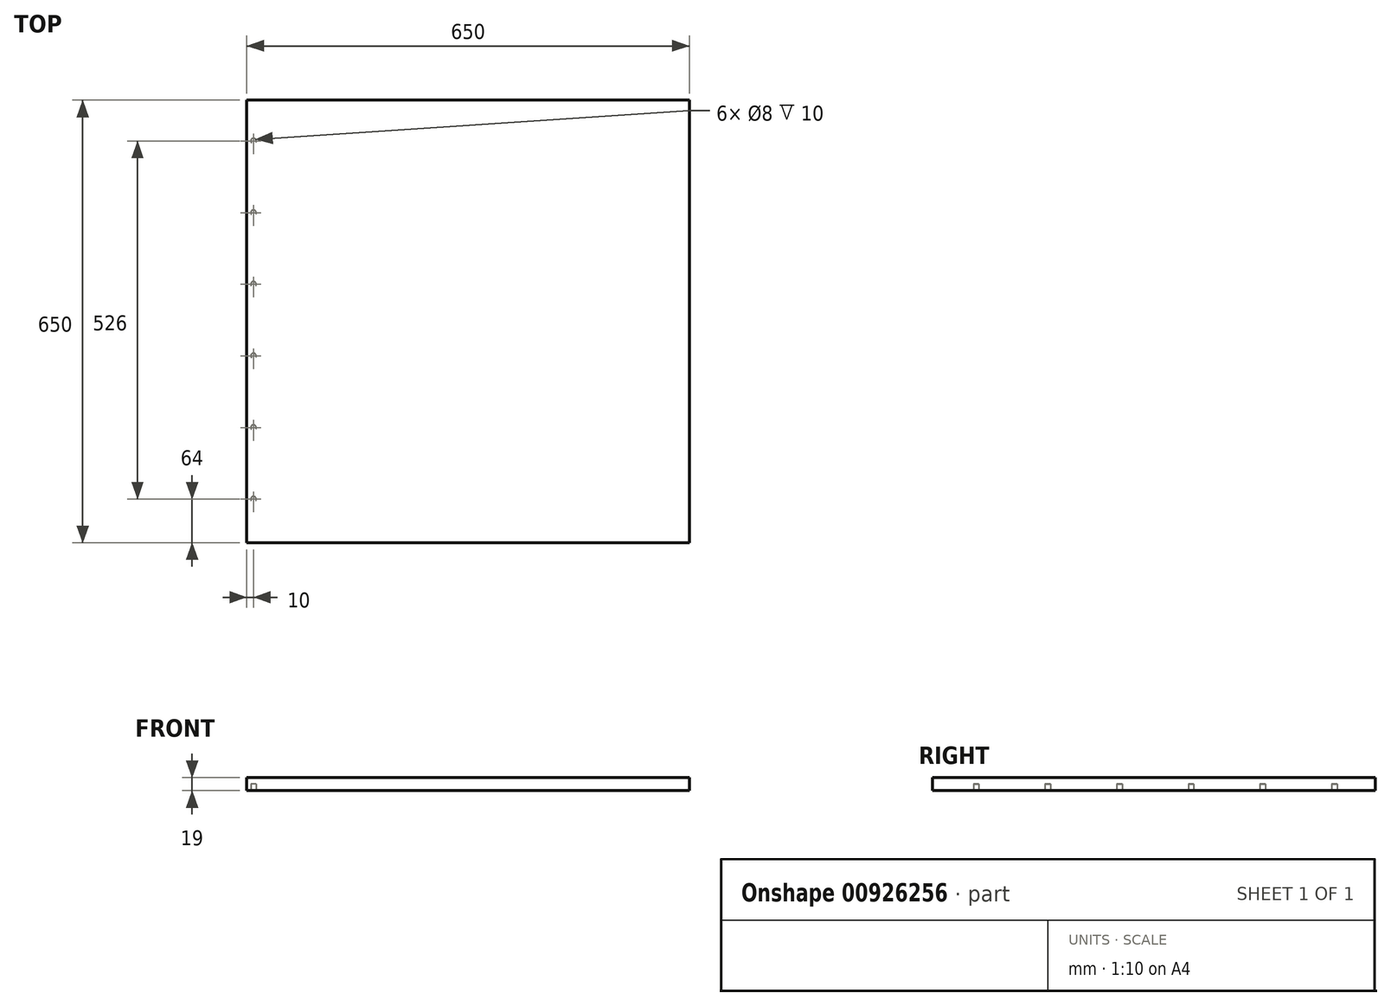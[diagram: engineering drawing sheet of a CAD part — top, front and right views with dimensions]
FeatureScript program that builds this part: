
annotation { "Feature Type Name" : "Feature", "Feature Type Description" : "" }
export const myFeature = defineFeature(function(context is Context, id is Id, definition is map)
    precondition{}
    {
        {
            var Q0;
            Q0=qCreatedBy(makeId("Top.planeOp"),FACE);
            var sketch = newSketch(context, id + "F0", { "sketchPlane" : qUnion([Q0])});
            skLineSegment(sketch, "E0.bottom", {"start": v(325, -325) * mm, "end": v(-325, -325) * mm});
            skLineSegment(sketch, "E0.top", {"start": v(325, 325) * mm, "end": v(-325, 325) * mm});
            skLineSegment(sketch, "E0.left", {"start": v(325, -325) * mm, "end": v(325, 325) * mm});
            skLineSegment(sketch, "E0.right", {"start": v(-325, -325) * mm, "end": v(-325, 325) * mm});
            skPoint(sketch, "E0.middle", {"position": v(0, 0) * mm});
            skLineSegment(sketch, "E1.bottom", {"start": v(305, -305) * mm, "end": v(-305, -305) * mm, "construction": true});
            skLineSegment(sketch, "E1.top", {"start": v(305, 305) * mm, "end": v(-305, 305) * mm, "construction": true});
            skLineSegment(sketch, "E1.left", {"start": v(305, -305) * mm, "end": v(305, 305) * mm, "construction": true});
            skLineSegment(sketch, "E1.right", {"start": v(-305, -305) * mm, "end": v(-305, 305) * mm, "construction": true});
            skLineSegment(sketch, "E2", {"start": v(-305, 305) * mm, "end": v(-325, 305) * mm, "construction": true});
            skLineSegment(sketch, "E3", {"start": v(-305, -305) * mm, "end": v(-325, -305) * mm, "construction": true});
            skLineSegment(sketch, "E4", {"start": v(-315, 305) * mm, "end": v(-315, -305) * mm, "construction": true});
            skPoint(sketch, "E5", {"position": v(-315, 265) * mm});
            skCircle(sketch, "E6", {"center": v(-315, 265) * mm, "radius": 4 * mm});
            skCircle(sketch, "E7.0.1.0", {"center": v(-315, 159.8) * mm, "radius": 4 * mm});
            skCircle(sketch, "E7.0.2.0", {"center": v(-315, 54.6) * mm, "radius": 4 * mm});
            skCircle(sketch, "E7.0.3.0", {"center": v(-315, -50.6) * mm, "radius": 4 * mm});
            skCircle(sketch, "E7.0.4.0", {"center": v(-315, -155.8) * mm, "radius": 4 * mm});
            skCircle(sketch, "E7.0.5.0", {"center": v(-315, -261) * mm, "radius": 4 * mm});
            skLineSegment(sketch, "E7.direction1", {"start": v(-315, 265) * mm, "end": v(-315, 265) * mm});
            skLineSegment(sketch, "E7.direction2", {"start": v(-315, 265) * mm, "end": v(-315, 159.8) * mm, "construction": true});
            skSolve(sketch);
        }
        {
            var Q0;
            Q0=makeQuery(id+"F0.imprint","IMPRINT",FACE,{"disambiguationData":[TD([[makeQuery(id+"F0.imprint","IMPRINT",EDGE,{"derivedFrom":sQuery(id+"F0.wireOp",EDGE,"E6")}),1.0]])]});
            var Q1;
            Q1=makeQuery(id+"F0.imprint","IMPRINT",FACE,{"disambiguationData":[TD([[makeQuery(id+"F0.imprint","IMPRINT",EDGE,{"derivedFrom":sQuery(id+"F0.wireOp",EDGE,"E7.0.1.0")}),1.0]])]});
            var Q2;
            Q2=makeQuery(id+"F0.imprint","IMPRINT",FACE,{"disambiguationData":[TD([[makeQuery(id+"F0.imprint","IMPRINT",EDGE,{"derivedFrom":sQuery(id+"F0.wireOp",EDGE,"E7.0.2.0")}),1.0]])]});
            var Q3;
            Q3=makeQuery(id+"F0.imprint","IMPRINT",FACE,{"disambiguationData":[TD([[makeQuery(id+"F0.imprint","IMPRINT",EDGE,{"derivedFrom":sQuery(id+"F0.wireOp",EDGE,"E7.0.3.0")}),1.0]])]});
            var Q4;
            Q4=makeQuery(id+"F0.imprint","IMPRINT",FACE,{"disambiguationData":[TD([[makeQuery(id+"F0.imprint","IMPRINT",EDGE,{"derivedFrom":sQuery(id+"F0.wireOp",EDGE,"E7.0.4.0")}),1.0]])]});
            var Q5;
            Q5=makeQuery(id+"F0.imprint","IMPRINT",FACE,{"disambiguationData":[TD([[makeQuery(id+"F0.imprint","IMPRINT",EDGE,{"derivedFrom":sQuery(id+"F0.wireOp",EDGE,"E0.bottom")}),-1.0]])]});
            var Q6;
            Q6=makeQuery(id+"F0.imprint","IMPRINT",FACE,{"disambiguationData":[TD([[makeQuery(id+"F0.imprint","IMPRINT",EDGE,{"derivedFrom":sQuery(id+"F0.wireOp",EDGE,"E7.0.5.0")}),1.0]])]});
            extrude(context, id + "F1", {"entities" : qUnion([Q0, Q1, Q2, Q3, Q4, Q5, Q6]), "depth" : 19 * mm, "offsetDistance" : 25 * mm});
        }
        {
            var Q0;
            Q0=makeQuery(id+"F0.imprint","IMPRINT",FACE,{"disambiguationData":[TD([[makeQuery(id+"F0.imprint","IMPRINT",EDGE,{"derivedFrom":sQuery(id+"F0.wireOp",EDGE,"E6")}),1.0]])]});
            var Q1;
            Q1=makeQuery(id+"F0.imprint","IMPRINT",FACE,{"disambiguationData":[TD([[makeQuery(id+"F0.imprint","IMPRINT",EDGE,{"derivedFrom":sQuery(id+"F0.wireOp",EDGE,"E7.0.1.0")}),1.0]])]});
            var Q2;
            Q2=makeQuery(id+"F0.imprint","IMPRINT",FACE,{"disambiguationData":[TD([[makeQuery(id+"F0.imprint","IMPRINT",EDGE,{"derivedFrom":sQuery(id+"F0.wireOp",EDGE,"E7.0.2.0")}),1.0]])]});
            var Q3;
            Q3=makeQuery(id+"F0.imprint","IMPRINT",FACE,{"disambiguationData":[TD([[makeQuery(id+"F0.imprint","IMPRINT",EDGE,{"derivedFrom":sQuery(id+"F0.wireOp",EDGE,"E7.0.3.0")}),1.0]])]});
            var Q4;
            Q4=makeQuery(id+"F0.imprint","IMPRINT",FACE,{"disambiguationData":[TD([[makeQuery(id+"F0.imprint","IMPRINT",EDGE,{"derivedFrom":sQuery(id+"F0.wireOp",EDGE,"E7.0.4.0")}),1.0]])]});
            var Q5;
            Q5=makeQuery(id+"F0.imprint","IMPRINT",FACE,{"disambiguationData":[TD([[makeQuery(id+"F0.imprint","IMPRINT",EDGE,{"derivedFrom":sQuery(id+"F0.wireOp",EDGE,"E7.0.5.0")}),1.0]])]});
            extrude(context, id + "F2", {"entities" : qUnion([Q0, Q1, Q2, Q3, Q4, Q5]), "operationType" : NewBodyOperationType.REMOVE, "depth" : 10 * mm, "offsetDistance" : 25 * mm});
        }
    });
